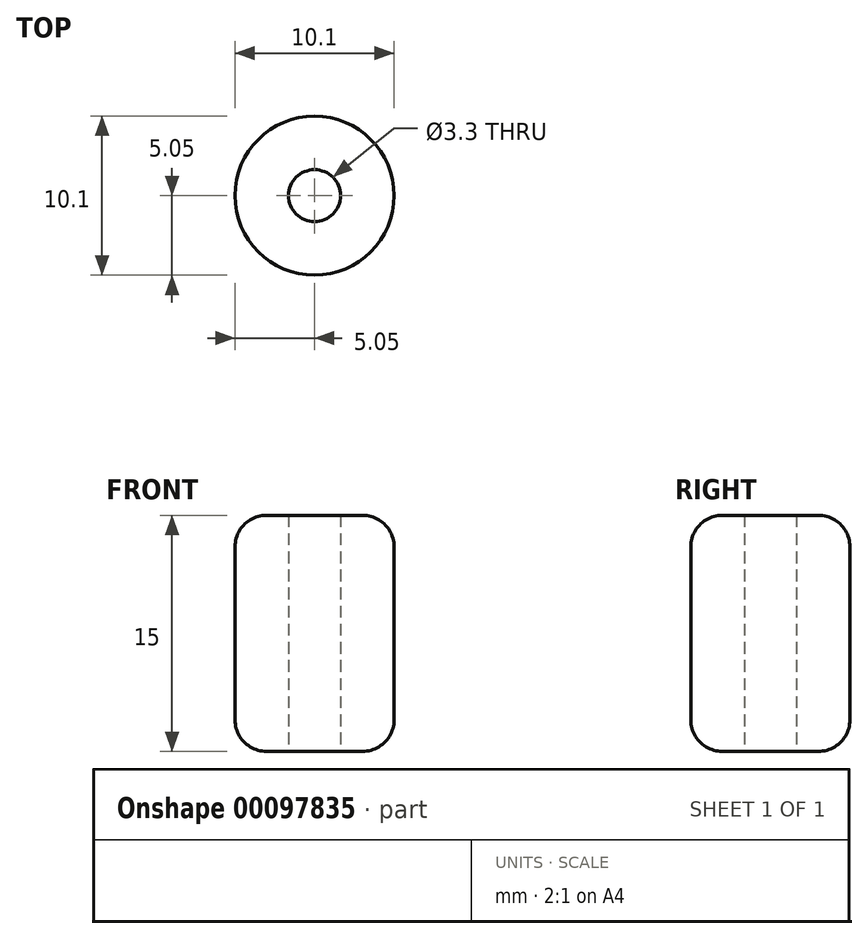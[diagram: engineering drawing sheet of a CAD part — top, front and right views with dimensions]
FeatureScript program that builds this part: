
annotation { "Feature Type Name" : "Feature", "Feature Type Description" : "" }
export const myFeature = defineFeature(function(context is Context, id is Id, definition is map)
    precondition{}
    {
        {
            var Q0;
            Q0=qCreatedBy(makeId("Top.planeOp"),FACE);
            var sketch = newSketch(context, id + "F0", { "sketchPlane" : qUnion([Q0])});
            skCircle(sketch, "E0", {"center": v(0, 0) * mm, "radius": 5.05 * mm});
            skCircle(sketch, "E1", {"center": v(0, 0) * mm, "radius": 1.65 * mm});
            skSolve(sketch);
        }
        {
            var Q0;
            Q0=qSketchRegion(id+"F0",true);
            extrude(context, id + "F1", {"entities" : qUnion([Q0]), "depth" : 15 * mm});
        }
        {
            var Q0;
            Q0=makeQuery(id+"F1.opExtrude","CAP_EDGE",EDGE,{"disambiguationData":[OSD([sQuery(id+"F0.wireOp",EDGE,"E0")])],"isStart":false});
            var Q1;
            Q1=makeQuery(id+"F1.opExtrude","CAP_EDGE",EDGE,{"disambiguationData":[OSD([sQuery(id+"F0.wireOp",EDGE,"E0")])],"isStart":true});
            fillet(context, id + "F2", {"entities" : qUnion([Q0, Q1]), "radius" : 2 * mm, "tangentPropagation" : true, "allowEdgeOverflow" : false});
        }
    });
